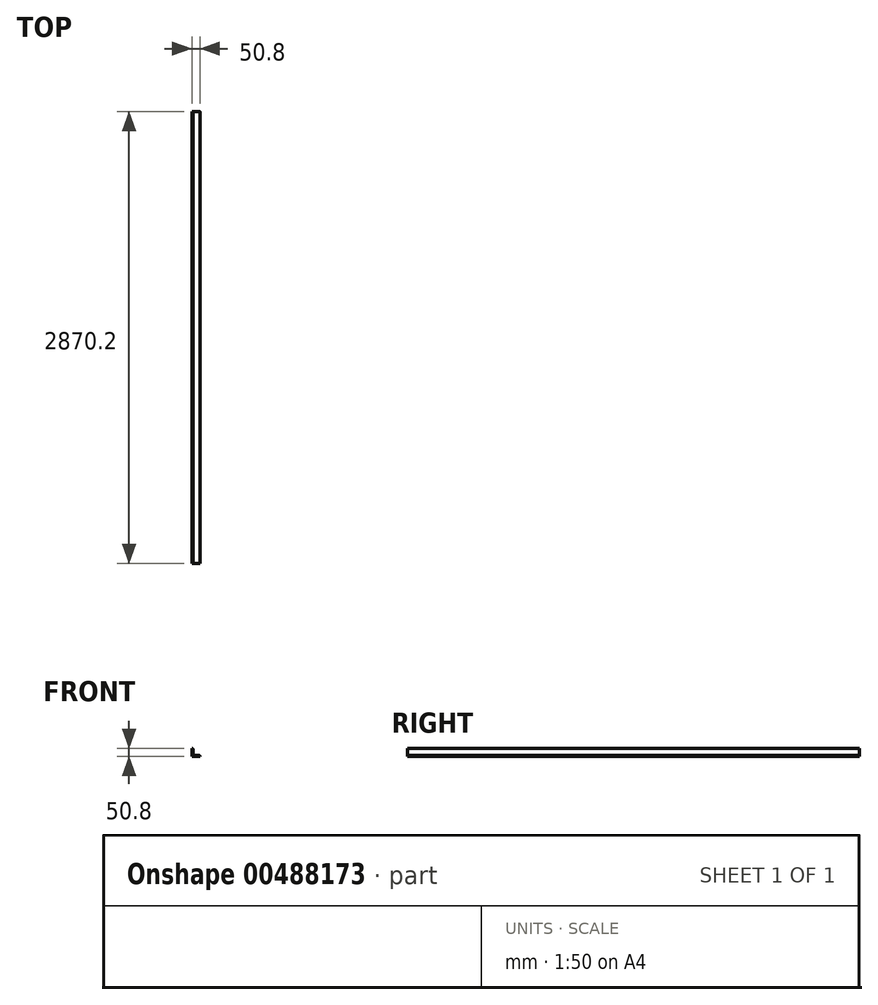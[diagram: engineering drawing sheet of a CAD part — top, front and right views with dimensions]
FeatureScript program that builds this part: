
annotation { "Feature Type Name" : "Feature", "Feature Type Description" : "" }
export const myFeature = defineFeature(function(context is Context, id is Id, definition is map)
    precondition{}
    {
        {
            var Q0;
            Q0=qCreatedBy(makeId("Front.planeOp"),FACE);
            var sketch = newSketch(context, id + "F0", { "sketchPlane" : qUnion([Q0])});
            skLineSegment(sketch, "E0", {"start": v(0, 0) * mm, "end": v(0, 50.8) * mm});
            skLineSegment(sketch, "E1", {"start": v(0, 0) * mm, "end": v(50.8, 0) * mm});
            skLineSegment(sketch, "E2", {"start": v(0, 50.8) * mm, "end": v(0, 50.8) * mm});
            skLineSegment(sketch, "E3", {"start": v(50.8, 0) * mm, "end": v(50.8, 0) * mm});
            skLineSegment(sketch, "E4", {"start": v(44.45, 6.35) * mm, "end": v(6.35, 6.35) * mm});
            skLineSegment(sketch, "E5", {"start": v(6.35, 44.45) * mm, "end": v(6.35, 6.35) * mm});
            skPoint(sketch, "E6.visualSharp", {"position": v(6.35, 50.8) * mm});
            skArc(sketch, "E6.filletArc", {"start": v(6.35, 44.45) * mm, "mid": v(4.5, 48.94) * mm, "end": v(0, 50.8) * mm});
            skPoint(sketch, "E7.visualSharp", {"position": v(50.8, 6.35) * mm});
            skArc(sketch, "E7.filletArc", {"start": v(50.8, 0) * mm, "mid": v(48.94, 4.5) * mm, "end": v(44.45, 6.35) * mm});
            skSolve(sketch);
        }
        {
            var Q0;
            Q0=makeQuery(id+"F0.imprint","IMPRINT",FACE,{"disambiguationData":[TD([[makeQuery(id+"F0.imprint","IMPRINT",EDGE,{"derivedFrom":sQuery(id+"F0.wireOp",EDGE,"E0")}),-1.0]])]});
            extrude(context, id + "F1", {"entities" : qUnion([Q0]), "depth" : 2730.5 * mm + 139.7 * mm, "offsetDistance" : 25.4 * mm});
        }
    });
